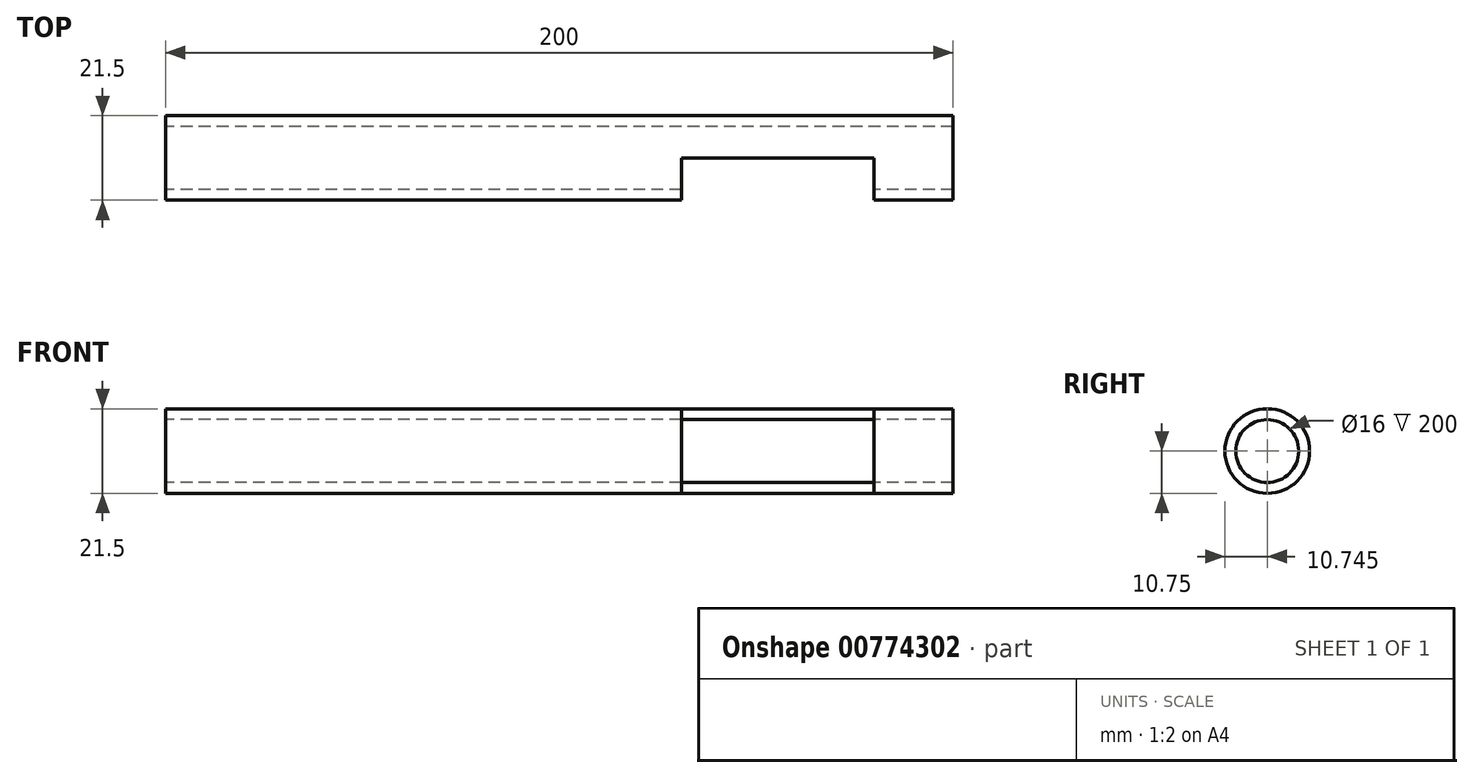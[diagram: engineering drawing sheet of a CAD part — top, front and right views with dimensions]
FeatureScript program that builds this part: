
annotation { "Feature Type Name" : "Feature", "Feature Type Description" : "" }
export const myFeature = defineFeature(function(context is Context, id is Id, definition is map)
    precondition{}
    {
        {
            var Q0;
            Q0=qCreatedBy(makeId("Top.planeOp"),FACE);
            var sketch = newSketch(context, id + "F0", { "sketchPlane" : qUnion([Q0])});
            skLineSegment(sketch, "E0.bottom", {"start": v(-58.8, 2.54) * mm, "end": v(141.2, 2.54) * mm});
            skLineSegment(sketch, "E0.top", {"start": v(-58.8, -8.21) * mm, "end": v(141.2, -8.21) * mm});
            skLineSegment(sketch, "E0.left", {"start": v(-58.8, 2.54) * mm, "end": v(-58.8, -8.21) * mm});
            skLineSegment(sketch, "E0.right", {"start": v(141.2, 2.54) * mm, "end": v(141.2, -8.21) * mm});
            skLineSegment(sketch, "E1", {"start": v(72.2, 2.54) * mm, "end": v(72.2, -8.21) * mm});
            skLineSegment(sketch, "E2", {"start": v(121.2, 2.54) * mm, "end": v(121.2, -8.21) * mm});
            skSolve(sketch);
        }
        {
            var Q0;
            Q0=makeQuery(id+"F0.imprint","IMPRINT",FACE,{"disambiguationData":[TD([[makeQuery(id+"F0.imprint","IMPRINT",EDGE,{"derivedFrom":sQuery(id+"F0.wireOp",EDGE,"E0.bottom")}),-1.0]])]});
            var Q1;
            Q1=sQuery(id+"F0.wireOp",EDGE,"E0.bottom");
            revolve(context, id + "F1", {"surfaceOperationType" : NewSurfaceOperationType.NEW, "entities" : qUnion([Q0]), "axis" : qUnion([Q1]), "revolveType" : RevolveType.FULL});
        }
        {
            var Q0;
            Q0=makeQuery(id+"F1.opRevolve","SWEPT_FACE",FACE,{"disambiguationData":[OSD([sQuery(id+"F0.wireOp",EDGE,"E0.left")])]});
            var sketch = newSketch(context, id + "F2", { "sketchPlane" : qUnion([Q0])});
            skCircle(sketch, "E3", {"center": v(-2.54, 0) * mm, "radius": 8 * mm});
            skSolve(sketch);
        }
        {
            var Q0;
            Q0=makeQuery(id+"F2.imprint","IMPRINT",FACE,{"disambiguationData":[TD([[makeQuery(id+"F2.imprint","IMPRINT",EDGE,{"derivedFrom":sQuery(id+"F2.wireOp",EDGE,"E3")}),1.0]])]});
            extrude(context, id + "F3", {"entities" : qUnion([Q0]), "operationType" : NewBodyOperationType.REMOVE, "oppositeDirection" : true, "depth" : 300 * mm, "offsetDistance" : 25 * mm});
        }
        {
            var Q0;
            {var subQ0=sQuery(id+"F0.wireOp",EDGE,"E1");Q0=makeQuery(id+"F0.imprint","IMPRINT",FACE,{"disambiguationData":[TD([[makeQuery(id+"F0.imprint","IMPRINT",EDGE,{"derivedFrom":subQ0}),1.0]])]});}
            extrude(context, id + "F4", {"entities" : qUnion([Q0]), "operationType" : NewBodyOperationType.REMOVE, "endBound" : BoundingType.SYMMETRIC, "oppositeDirection" : true, "depth" : 26 * mm, "offsetDistance" : 25 * mm});
        }
        {
            var Q0;
            Q0=makeQuery(id+"F4.boolean.opBoolean","COPY",FACE,{"disambiguationData":[OD(0.0)],"derivedFrom":makeQuery(id+"F4.opExtrude","SWEPT_FACE",FACE,{"disambiguationData":[OSD([sQuery(id+"F0.wireOp",EDGE,"E0.bottom")])]})});
            var sketch = newSketch(context, id + "F5", { "sketchPlane" : qUnion([Q0])});
            skLineSegment(sketch, "E4", {"start": v(126.2, -8) * mm, "end": v(126.2, 8.2) * mm});
            skPoint(sketch, "E5", {"position": v(126.2, 0) * mm});
            skLineSegment(sketch, "E6", {"start": v(117.31, 0) * mm, "end": v(135.07, 0) * mm});
            skSolve(sketch);
        }
        {
            var Q0;
            Q0=makeQuery(id+"F4.boolean.opBoolean","COPY",FACE,{"disambiguationData":[OD(1.0)],"derivedFrom":makeQuery(id+"F4.opExtrude","SWEPT_FACE",FACE,{"disambiguationData":[OSD([sQuery(id+"F0.wireOp",EDGE,"E0.bottom")])]})});
            var sketch = newSketch(context, id + "F6", { "sketchPlane" : qUnion([Q0])});
            skLineSegment(sketch, "E7", {"start": v(96.7, 10.75) * mm, "end": v(96.7, -10.74) * mm});
            skLineSegment(sketch, "E8", {"start": v(87.48, 0) * mm, "end": v(105.9, 0) * mm});
            skPoint(sketch, "E9", {"position": v(96.7, 0) * mm});
            skSolve(sketch);
        }
    });
